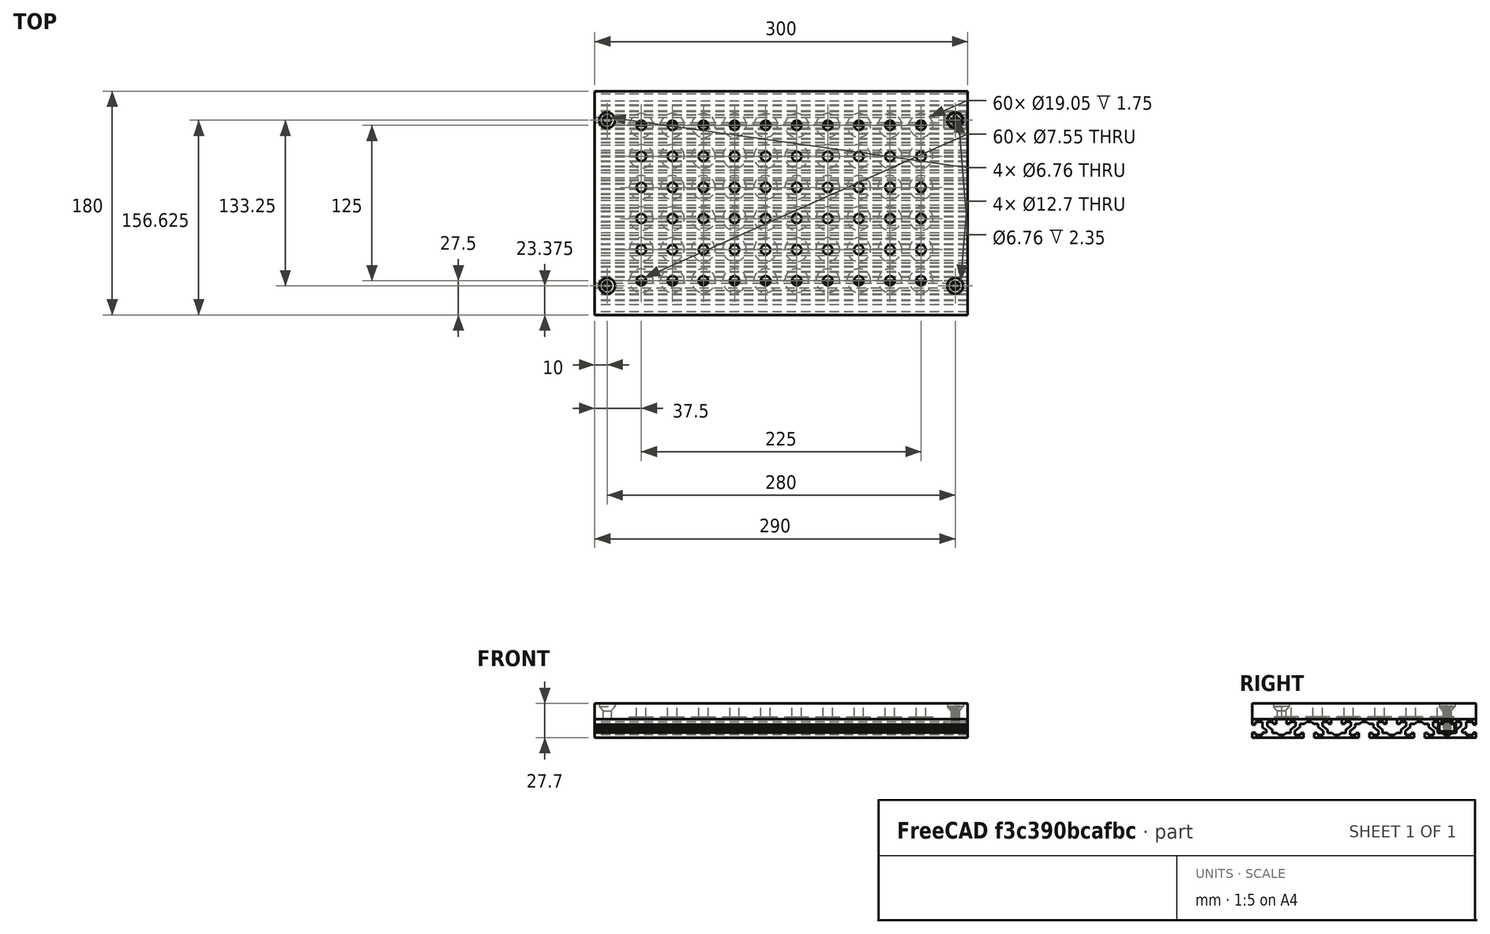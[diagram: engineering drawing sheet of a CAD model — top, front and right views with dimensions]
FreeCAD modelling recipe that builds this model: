
FCSTD DOCUMENT  (FreeCAD 1.0R39109 (Git))
Label: wasteboard
License: All rights reserved
LicenseURL: http://en.wikipedia.org/wiki/All_rights_reserved
objects: Sketcher::SketchObject×11, TechDraw::DrawViewDimension×9, PartDesign::Pocket×5, PartDesign::Pad×4, PartDesign::LinearPattern×4, PartDesign::Chamfer×4, PartDesign::Mirrored×3, PartDesign::Body×3, TechDraw::DrawProjGroupItem×3, PartDesign::Hole×2, PartDesign::MultiTransform×2, TechDraw::DrawSVGTemplate×2, TechDraw::DrawPage×2, Part::Feature×1, PartDesign::ShapeBinder×1, PartDesign::Plane×1, App::Part×1, PartDesign::SubShapeBinder×1, TechDraw::DrawProjGroup×1
note: 110 computed .brp shape members not serialized (recipe doc carries the construction recipe); baked Part::Feature solids carry a one-line shape summary decoded from their .brp

FEATURE [Sketcher::SketchObject] Sketch001
  ArcFitTolerance = 0
  AttachmentSupport = -> [YZ_Plane001]
  FullyConstrained = true
  MakeInternals = false
  MapMode = 5
  Placement = pos=(0,0,0) rot=(0.57735,0.57735,0.57735;2.0944rad)
  sketch-geometry (4):
    g0: LineSegment StartX=-90 StartY=7.5 StartZ=0 EndX=90 EndY=7.5 EndZ=0
    g1: LineSegment StartX=90 StartY=7.5 StartZ=0 EndX=90 EndY=-7.5 EndZ=0
    g2: LineSegment StartX=90 StartY=-7.5 StartZ=0 EndX=-90 EndY=-7.5 EndZ=0
    g3: LineSegment StartX=-90 StartY=-7.5 StartZ=0 EndX=-90 EndY=7.5 EndZ=0
  constraints (10):
    c: Coincident(g0,g1)
    c: Coincident(g1,g2)
    c: Coincident(g2,g3)
    c: Coincident(g3,g0)
    c: Horizontal(g2)
    c: Vertical(g3)
    c: Symmetric(g0,g0,g-2)
    c: Symmetric(g0,g1,g-1)
    c: DistanceX(g0,g0) = 180
    c: DistanceY(g3,g3) = 15
FEATURE [PartDesign::Pad] Pad001
  AllowMultiFace = false
  Direction = (1,0,0)
  Length = 300
  Length2 = 100
  Midplane = true
  Placement = pos=(0,0,0) rot=(0.57735,0.57735,0.57735;2.0944rad)
  Profile = -> Sketch001
  Refine = true
  Suppressed = false
  Type = 0
FEATURE [Sketcher::SketchObject] Sketch002
  ArcFitTolerance = 0
  AttachmentSupport = -> [Pad001]
  ExternalGeometry = -> [Pad001]
  FullyConstrained = true
  MakeInternals = false
  MapMode = 5
  Placement = pos=(150,0,0) rot=(0.57735,0.57735,0.57735;2.0944rad)
  sketch-geometry (14):
    g0: LineSegment StartX=-90 StartY=3.175 StartZ=0 EndX=-87.6 EndY=3.175 EndZ=0
    g1: LineSegment StartX=-87.6 StartY=-3.175 StartZ=0 EndX=-90 EndY=-3.175 EndZ=0
    g2: LineSegment StartX=-90 StartY=-3.175 StartZ=0 EndX=-90 EndY=3.175 EndZ=0
    g3: LineSegment StartX=-87.6 StartY=5.1 StartZ=0 EndX=-82 EndY=5.1 EndZ=0
    g4: LineSegment StartX=-82 StartY=5.1 StartZ=0 EndX=-82 EndY=0.9 EndZ=0
    g5: LineSegment StartX=-82 StartY=-5.1 StartZ=0 EndX=-87.6 EndY=-5.1 EndZ=0
    g6: LineSegment StartX=-87.6 StartY=-5.1 StartZ=0 EndX=-87.6 EndY=-3.175 EndZ=0
    g7: LineSegment StartX=-87.6 StartY=3.175 StartZ=0 EndX=-87.6 EndY=5.1 EndZ=0
    g8: LineSegment [constr] StartX=-87.6 StartY=3.175 StartZ=0 EndX=-87.6 EndY=-3.175 EndZ=0
    g9: LineSegment StartX=-82 StartY=0.9 StartZ=0 EndX=-78.75 EndY=-1.425 EndZ=0
    g10: LineSegment StartX=-78.75 StartY=-1.425 StartZ=0 EndX=-78.75 EndY=-3.175 EndZ=0
    g11: LineSegment StartX=-78.75 StartY=-3.175 StartZ=0 EndX=-82 EndY=-3.175 EndZ=0
    g12: LineSegment StartX=-82 StartY=-3.175 StartZ=0 EndX=-82 EndY=-5.1 EndZ=0
    g13: LineSegment [constr] StartX=-82 StartY=-3.175 StartZ=0 EndX=-87.6 EndY=-3.175 EndZ=0
  constraints (37):
    c: Coincident(g1,g2)
    c: Coincident(g2,g0)
    c: Horizontal(g0)
    c: Horizontal(g1)
    c: Coincident(g3,g4)
    c: Coincident(g12,g5)
    c: Coincident(g5,g6)
    c: Coincident(g7,g3)
    c: Horizontal(g3)
    c: Horizontal(g5)
    c: Vertical(g6)
    c: Coincident(g7,g0)
    c: Vertical(g7)
    c: Coincident(g6,g1)
    c: Symmetric(g0,g1,g-1)
    c: PointOnObject(g0,g-3)
    c: DistanceY(g2,g2) = 6.35
    c: DistanceX(g0,g0) = 2.4
    c: Coincident(g8,g0)
    c: Coincident(g8,g1)
    c: Vertical(g8)
    c: Symmetric(g3,g12,g-1)
    c: DistanceY(g3,g-3) = 2.4
    c: DistanceX(g-3,g3) = 8
    c: Coincident(g10,g9)
    c: Vertical(g10)
    c: Coincident(g11,g10)
    c: Coincident(g4,g9)
    c: Coincident(g12,g11)
    c: Tangent(g4,g12)
    c: DistanceX(g0,g9) = 11.25
    c: DistanceY(g10,g10) = 1.75
    c: Horizontal(g11)
    c: DistanceY(g4,g4) = 4.2
    c: Coincident(g13,g11)
    c: Coincident(g13,g1)
    c: Horizontal(g13)
FEATURE [PartDesign::Pocket] Pocket
  AllowMultiFace = false
  BaseFeature = -> Pad001
  Direction = (-1,0,0)
  Length = 5
  Length2 = 100
  Placement = pos=(0,0,0) rot=(0.57735,0.57735,0.57735;2.0944rad)
  Profile = -> Sketch002
  Refine = true
  Suppressed = false
  Type = 1
FEATURE [PartDesign::Mirrored] Mirrored
  BaseFeature = -> Pocket
  MirrorPlane = -> XZ_Plane001
  Originals = -> [Pocket]
  Placement = pos=(0,0,0) rot=(0.57735,0.57735,0.57735;2.0944rad)
  Refine = true
  Suppressed = false
  TransformMode = 0
FEATURE [Sketcher::SketchObject] Sketch003
  ArcFitTolerance = 0
  AttachmentSupport = -> [Mirrored]
  ExternalGeometry = -> [Mirrored]
  FullyConstrained = true
  MakeInternals = false
  MapMode = 5
  Placement = pos=(150,0,0) rot=(0.57735,0.57735,0.57735;2.0944rad)
  sketch-geometry (28):
    g0: LineSegment StartX=-70.875 StartY=7.5 StartZ=0 EndX=-70.875 EndY=3.5 EndZ=0
    g1: LineSegment StartX=-70.875 StartY=3.5 StartZ=0 EndX=-73.275 EndY=3.5 EndZ=0
    g2: LineSegment StartX=-73.275 StartY=3.5 StartZ=0 EndX=-73.275 EndY=5.1 EndZ=0
    g3: LineSegment StartX=-73.275 StartY=5.1 StartZ=0 EndX=-78 EndY=5.1 EndZ=0
    g4: LineSegment StartX=-78 StartY=5.1 StartZ=0 EndX=-78 EndY=2.1 EndZ=0
    g5: LineSegment StartX=-78 StartY=2.1 StartZ=0 EndX=-74 EndY=-0.972 EndZ=0
    g6: LineSegment StartX=-74 StartY=-0.972 StartZ=0 EndX=-74 EndY=-3.75 EndZ=0
    g7: LineSegment StartX=-74 StartY=-3.75 StartZ=0 EndX=-70.3828 EndY=-3.75 EndZ=0
    g8: LineSegment StartX=-70.3828 StartY=-3.75 StartZ=0 EndX=-68.625 EndY=-5.1 EndZ=0
    g9: LineSegment StartX=-68.625 StartY=-5.1 StartZ=0 EndX=-64.625 EndY=-5.1 EndZ=0
    g10: LineSegment StartX=-62.375 StartY=7.5 StartZ=0 EndX=-70.875 EndY=7.5 EndZ=0
    g11: LineSegment StartX=-62.375 StartY=7.5 StartZ=0 EndX=-62.375 EndY=3.5 EndZ=0
    g12: LineSegment StartX=-62.375 StartY=3.5 StartZ=0 EndX=-59.975 EndY=3.5 EndZ=0
    g13: LineSegment StartX=-59.975 StartY=3.5 StartZ=0 EndX=-59.975 EndY=5.1 EndZ=0
    g14: LineSegment StartX=-59.975 StartY=5.1 StartZ=0 EndX=-55.25 EndY=5.1 EndZ=0
    g15: LineSegment StartX=-55.25 StartY=5.1 StartZ=0 EndX=-55.25 EndY=2.1 EndZ=0
    g16: LineSegment StartX=-55.25 StartY=2.1 StartZ=0 EndX=-59.25 EndY=-0.972 EndZ=0
    g17: LineSegment StartX=-59.25 StartY=-0.972 StartZ=0 EndX=-59.25 EndY=-3.75 EndZ=0
    g18: LineSegment StartX=-59.25 StartY=-3.75 StartZ=0 EndX=-62.8672 EndY=-3.75 EndZ=0
    g19: LineSegment StartX=-62.8672 StartY=-3.75 StartZ=0 EndX=-64.625 EndY=-5.1 EndZ=0
    g20: LineSegment [constr] StartX=-70.3828 StartY=-3.75 StartZ=0 EndX=-62.8672 EndY=-3.75 EndZ=0
    g21: LineSegment [constr] StartX=-70.875 StartY=3.5 StartZ=0 EndX=-62.375 EndY=3.5 EndZ=0
    g22: LineSegment [constr] StartX=-78 StartY=2.1 StartZ=0 EndX=-55.25 EndY=2.1 EndZ=0
    g23: LineSegment [constr] StartX=-59.975 StartY=5.1 StartZ=0 EndX=-73.275 EndY=5.1 EndZ=0
    g24: LineSegment [constr] StartX=-74 StartY=-0.972 StartZ=0 EndX=-59.25 EndY=-0.972 EndZ=0
    g25: LineSegment [constr] StartX=-66.625 StartY=7.5 StartZ=0 EndX=-66.625 EndY=-5.1 EndZ=0
    g26: LineSegment [constr] StartX=-70.3828 StartY=-3.75 StartZ=0 EndX=-74 EndY=-0.972 EndZ=0
    g27: LineSegment [constr] StartX=-62.8672 StartY=-3.75 StartZ=0 EndX=-59.25 EndY=-0.972 EndZ=0
  constraints (76):
    c: PointOnObject(g0,g-3)
    c: Coincident(g1,g0)
    c: Horizontal(g1)
    c: Coincident(g2,g1)
    c: Coincident(g3,g2)
    c: Horizontal(g3)
    c: Coincident(g4,g3)
    c: Coincident(g5,g4)
    c: Coincident(g6,g5)
    c: Coincident(g7,g6)
    c: Coincident(g8,g7)
    c: Coincident(g9,g8)
    c: Horizontal(g9)
    c: PointOnObject(g10,g-3)
    c: Coincident(g10,g0)
    c: Vertical(g0)
    c: Vertical(g2)
    c: Vertical(g6)
    c: Horizontal(g7)
    c: Coincident(g11,g10)
    c: Vertical(g11)
    c: Coincident(g12,g11)
    c: Coincident(g13,g12)
    c: Coincident(g14,g13)
    c: Horizontal(g14)
    c: Coincident(g15,g14)
    c: Vertical(g15)
    c: Coincident(g16,g15)
    c: Coincident(g17,g16)
    c: Vertical(g17)
    c: Coincident(g18,g17)
    c: Horizontal(g18)
    c: Coincident(g19,g18)
    c: Coincident(g19,g9)
    c: Coincident(g20,g7)
    c: Coincident(g20,g18)
    c: Horizontal(g20)
    c: Coincident(g21,g0)
    c: Coincident(g21,g11)
    c: Coincident(g22,g4)
    c: Coincident(g22,g15)
    c: Horizontal(g22)
    c: Coincident(g23,g13)
    c: Coincident(g23,g2)
    c: Horizontal(g23)
    c: Horizontal(g21)
    c: Horizontal(g12)
    c: Vertical(g13)
    c: Vertical(g4)
    c: Coincident(g24,g5)
    c: Coincident(g24,g16)
    c: Horizontal(g24)
    c: DistanceX(g2,g0) = 2.4
    c: Equal(g1,g12)
    c: Vertical(g25)
    c: Symmetric(g9,g8,g25)
    c: Symmetric(g10,g0,g25)
    c: DistanceY(g3,g0) = 2.4
    c: DistanceX(g10,g10) = 8.5
    c: DistanceX(g3,g14) = 22.75
    c: Equal(g14,g3)
    c: DistanceY(g0,g0) = 4
    c: DistanceX(g9,g9) = 4
    c: DistanceX(g6,g17) = 14.75
    c: Equal(g18,g7)
    c: Coincident(g26,g7)
    c: Coincident(g26,g5)
    c: Coincident(g27,g18)
    c: Coincident(g27,g16)
    c: Parallel(g27,g16)
    c: Parallel(g19,g27)
    c: Parallel(g26,g8)
    c: DistanceY(g-4,g8) = 2.4
    c: DistanceY(g4,g4) = 3
    c: DistanceY(g-4,g6) = 3.75
    c: DistanceX(g-5,g3) = 4
FEATURE [PartDesign::Pocket] Pocket001
  AllowMultiFace = false
  BaseFeature = -> Mirrored
  Direction = (-1,0,0)
  Length = 5
  Length2 = 100
  Placement = pos=(0,0,0) rot=(0.57735,0.57735,0.57735;2.0944rad)
  Profile = -> Sketch003
  Refine = true
  Suppressed = false
  Type = 1
FEATURE [PartDesign::LinearPattern] LinearPattern
  BaseFeature = -> Pocket001
  Direction = -> Sketch003 [H_Axis]
  Length = 133.25
  Mode = 0
  Occurrences = 4
  Offset = 44.4167
  Originals = -> [Pocket001]
  Placement = pos=(0,0,0) rot=(0.57735,0.57735,0.57735;2.0944rad)
  Refine = true
  Suppressed = false
  TransformMode = 0
FEATURE [Sketcher::SketchObject] Sketch004
  ArcFitTolerance = 0
  AttachmentSupport = -> [LinearPattern]
  ExternalGeometry = -> [LinearPattern]
  FullyConstrained = true
  MakeInternals = false
  MapMode = 5
  Placement = pos=(150,0,0) rot=(0.57735,0.57735,0.57735;2.0944rad)
  sketch-geometry (30):
    g0: LineSegment StartX=-48.6667 StartY=-7.5 StartZ=0 EndX=-48.6667 EndY=-3.5 EndZ=0
    g1: LineSegment StartX=-48.6667 StartY=-3.5 StartZ=0 EndX=-51.0667 EndY=-3.5 EndZ=0
    g2: LineSegment StartX=-51.0667 StartY=-3.5 StartZ=0 EndX=-51.0667 EndY=-5.1 EndZ=0
    g3: LineSegment StartX=-51.0667 StartY=-5.1 StartZ=0 EndX=-55.7917 EndY=-5.1 EndZ=0
    g4: LineSegment StartX=-55.7917 StartY=-5.1 StartZ=0 EndX=-55.7917 EndY=-2.1 EndZ=0
    g5: LineSegment StartX=-55.7917 StartY=-2.1 StartZ=0 EndX=-51.7917 EndY=0.972 EndZ=0
    g6: LineSegment StartX=-46.4167 StartY=5.1 StartZ=0 EndX=-42.4167 EndY=5.1 EndZ=0
    g7: LineSegment StartX=-42.4167 StartY=5.1 StartZ=0 EndX=-40.6589 EndY=3.75 EndZ=0
    g8: LineSegment StartX=-33.0417 StartY=-2.1 StartZ=0 EndX=-33.0417 EndY=-5.1 EndZ=0
    g9: LineSegment StartX=-33.0417 StartY=-5.1 StartZ=0 EndX=-37.7667 EndY=-5.1 EndZ=0
    g10: LineSegment StartX=-37.7667 StartY=-5.1 StartZ=0 EndX=-37.7667 EndY=-3.5 EndZ=0
    g11: LineSegment StartX=-37.7667 StartY=-3.5 StartZ=0 EndX=-40.1667 EndY=-3.5 EndZ=0
    g12: LineSegment StartX=-40.1667 StartY=-3.5 StartZ=0 EndX=-40.1667 EndY=-7.5 EndZ=0
    g13: LineSegment StartX=-40.1667 StartY=-7.5 StartZ=0 EndX=-48.6667 EndY=-7.5 EndZ=0
    g14: LineSegment [constr] StartX=-44.4167 StartY=-7.5 StartZ=0 EndX=-44.4167 EndY=5.1 EndZ=0
    g15: LineSegment [constr] StartX=-40.1667 StartY=-3.5 StartZ=0 EndX=-48.6667 EndY=-3.5 EndZ=0
    g16: LineSegment [constr] StartX=-37.7667 StartY=-5.1 StartZ=0 EndX=-51.0667 EndY=-5.1 EndZ=0
    g17: LineSegment [constr] StartX=-33.0417 StartY=-2.1 StartZ=0 EndX=-55.7917 EndY=-2.1 EndZ=0
    g18: LineSegment StartX=-51.7917 StartY=0.972 StartZ=0 EndX=-51.7917 EndY=3.75 EndZ=0
    g19: LineSegment StartX=-51.7917 StartY=3.75 StartZ=0 EndX=-48.1745 EndY=3.75 EndZ=0
    g20: LineSegment StartX=-37.0417 StartY=3.75 StartZ=0 EndX=-37.0417 EndY=0.972 EndZ=0
    g21: LineSegment [constr] StartX=-37.0417 StartY=0.972 StartZ=0 EndX=-51.7917 EndY=0.972 EndZ=0
    g22: LineSegment StartX=-37.0417 StartY=0.972 StartZ=0 EndX=-33.0417 EndY=-2.1 EndZ=0
    g23: LineSegment StartX=-48.1745 StartY=3.75 StartZ=0 EndX=-46.4167 EndY=5.1 EndZ=0
    g24: LineSegment StartX=-40.6589 StartY=3.75 StartZ=0 EndX=-37.0417 EndY=3.75 EndZ=0
    g25: LineSegment [constr] StartX=-48.1745 StartY=3.75 StartZ=0 EndX=-40.6589 EndY=3.75 EndZ=0
    g26: LineSegment [constr] StartX=-40.6589 StartY=3.75 StartZ=0 EndX=-37.0417 EndY=0.972 EndZ=0
    g27: LineSegment [constr] StartX=-48.1745 StartY=3.75 StartZ=0 EndX=-51.7917 EndY=0.972 EndZ=0
    g28: LineSegment [constr] StartX=-51.7917 StartY=3.75 StartZ=0 EndX=-55.25 EndY=3.75 EndZ=0
    g29: LineSegment [constr] StartX=-37.0417 StartY=3.75 StartZ=0 EndX=-33.5833 EndY=3.75 EndZ=0
  constraints (82):
    c: PointOnObject(g0,g-3)
    c: Coincident(g1,g0)
    c: Coincident(g2,g1)
    c: Coincident(g3,g2)
    c: Coincident(g4,g3)
    c: Coincident(g5,g4)
    c: Coincident(g6,g23)
    c: Coincident(g7,g6)
    c: Coincident(g8,g22)
    c: Vertical(g8)
    c: Coincident(g9,g8)
    c: Coincident(g10,g9)
    c: Coincident(g11,g10)
    c: Horizontal(g11)
    c: Coincident(g12,g11)
    c: PointOnObject(g12,g-3)
    c: Vertical(g12)
    c: Coincident(g13,g12)
    c: Coincident(g13,g0)
    c: Horizontal(g9)
    c: Horizontal(g3)
    c: Horizontal(g1)
    c: Vertical(g10)
    c: Vertical(g0)
    c: Vertical(g4)
    c: Horizontal(g6)
    c: Vertical(g2)
    c: Vertical(g14)
    c: Coincident(g15,g11)
    c: Coincident(g15,g0)
    c: Coincident(g16,g9)
    c: Coincident(g16,g2)
    c: Coincident(g17,g22)
    c: Coincident(g17,g4)
    c: Horizontal(g17)
    c: Horizontal(g15)
    c: Symmetric(g12,g0,g14)
    c: Symmetric(g6,g23,g14)
    c: DistanceX(g6,g6) = 4
    c: DistanceY(g23,g-4) = 2.4
    c: Equal(g9,g3)
    c: Equal(g2,g10)
    c: DistanceX(g11,g11) = 2.4
    c: DistanceY(g12,g12) = 4
    c: DistanceX(g3,g8) = 22.75
    c: Equal(g11,g1)
    c: DistanceY(g4,g4) = 3
    c: DistanceX(g13,g13) = 8.5
    c: DistanceY(g-3,g3) = 2.4
    c: Vertical(g18)
    c: Coincident(g19,g18)
    c: Horizontal(g19)
    c: Coincident(g20,g24)
    c: Vertical(g20)
    c: Horizontal(g21)
    c: Coincident(g22,g20)
    c: Coincident(g5,g18)
    c: Coincident(g24,g7)
    c: Coincident(g19,g23)
    c: Coincident(g21,g20)
    c: Coincident(g21,g5)
    c: Horizontal(g24)
    c: Coincident(g25,g19)
    c: Coincident(g25,g7)
    c: Horizontal(g25)
    c: Coincident(g26,g7)
    c: Coincident(g26,g20)
    c: Coincident(g27,g19)
    c: Coincident(g27,g5)
    c: Parallel(g27,g23)
    c: Parallel(g27,g5)
    c: Parallel(g7,g26)
    c: Parallel(g26,g22)
    c: DistanceX(g18,g20) = 14.75
    c: DistanceY(g18,g-4) = 3.75
    c: Coincident(g28,g18)
    c: PointOnObject(g28,g-6)
    c: Horizontal(g28)
    c: Coincident(g29,g20)
    c: PointOnObject(g29,g-5)
    c: Horizontal(g29)
    c: Equal(g29,g28)
FEATURE [PartDesign::Pocket] Pocket002
  AllowMultiFace = false
  BaseFeature = -> LinearPattern
  Direction = (-1,0,0)
  Length = 5
  Length2 = 100
  Placement = pos=(0,0,0) rot=(0.57735,0.57735,0.57735;2.0944rad)
  Profile = -> Sketch004
  Refine = true
  Suppressed = false
  Type = 1
FEATURE [PartDesign::LinearPattern] LinearPattern001
  BaseFeature = -> Pocket002
  Direction = -> Sketch004 [H_Axis]
  Length = 88.83
  Mode = 0
  Occurrences = 3
  Offset = 44.415
  Originals = -> [Pocket002]
  Placement = pos=(0,0,0) rot=(0.57735,0.57735,0.57735;2.0944rad)
  Refine = true
  Suppressed = false
  TransformMode = 0
FEATURE [PartDesign::Body] Body001  label="aluminum extruded bed"
  AllowCompound = false
  Group = -> [Sketch001,Pad001,Sketch002,Pocket,Mirrored,Sketch003,Pocket001,LinearPattern,Sketch004,Pocket002,LinearPattern001]
  Origin = -> Origin001
  Tip = -> LinearPattern001
FEATURE [Part::Feature] Part__Feature001  label="90273A540"
  Placement = pos=(140,66.62,14.05) rot=(0,0,1;0rad)
  shape: bbox 12.12 x 12.12 x 19.53 mm, 84 faces (baked)
FEATURE [PartDesign::ShapeBinder] ShapeBinder001
  Placement = pos=(0,0,0) rot=(0.57735,0.57735,0.57735;2.0944rad)
  Support = -> [LinearPattern001]
  TraceSupport = false
FEATURE [PartDesign::Plane] DatumPlane
  AttachmentOffset = pos=(0,0,-10) rot=(0,0,1;0rad)
  AttachmentSupport = -> [ShapeBinder001]
  Length = 60
  MapMode = 5
  Placement = pos=(140,0,0) rot=(0.57735,0.57735,0.57735;2.0944rad)
  ResizeMode = 0
  Width = 60
FEATURE [Sketcher::SketchObject] Sketch008
  ArcFitTolerance = 0
  AttachmentSupport = -> [DatumPlane]
  ExternalGeometry = -> [ShapeBinder001]
  FullyConstrained = true
  MakeInternals = false
  MapMode = 5
  Placement = pos=(140,0,0) rot=(0.57735,0.57735,0.57735;2.0944rad)
  sketch-geometry (8):
    g0: LineSegment StartX=62.525 StartY=5.5 StartZ=0 EndX=70.725 EndY=5.5 EndZ=0
    g1: LineSegment StartX=70.725 StartY=5.5 StartZ=0 EndX=70.725 EndY=3.5 EndZ=0
    g2: LineSegment StartX=62.525 StartY=3.5 StartZ=0 EndX=62.525 EndY=5.5 EndZ=0
    g3: LineSegment StartX=59.4 StartY=3.5 StartZ=0 EndX=62.525 EndY=3.5 EndZ=0
    g4: LineSegment StartX=73.85 StartY=3.5 StartZ=0 EndX=73.85 EndY=-3 EndZ=0
    g5: LineSegment StartX=73.85 StartY=-3 StartZ=0 EndX=59.4 EndY=-3 EndZ=0
    g6: LineSegment StartX=59.4 StartY=-3 StartZ=0 EndX=59.4 EndY=3.5 EndZ=0
    g7: LineSegment StartX=70.725 StartY=3.5 StartZ=0 EndX=73.85 EndY=3.5 EndZ=0
  constraints (24):
    c: Coincident(g0,g1)
    c: Coincident(g2,g0)
    c: Horizontal(g0)
    c: Vertical(g1)
    c: Vertical(g2)
    c: Coincident(g7,g4)
    c: Coincident(g4,g5)
    c: Coincident(g5,g6)
    c: Coincident(g6,g3)
    c: Horizontal(g3)
    c: Horizontal(g5)
    c: Vertical(g4)
    c: Vertical(g6)
    c: Coincident(g3,g2)
    c: Coincident(g7,g1)
    c: DistanceX(g0,g-3) = 0.15
    c: DistanceX(g-4,g0) = 0.15
    c: DistanceX(g-7,g5) = 0.15
    c: DistanceX(g4,g-8) = 0.15
    c: PointOnObject(g-6,g7)
    c: PointOnObject(g-5,g3)
    c: DistanceY(g-8,g4) = 0.75
    c: Horizontal(g7)
    c: DistanceY(g0,g-3) = 2
FEATURE [PartDesign::Pad] Pad002
  AllowMultiFace = false
  Direction = (1,0,0)
  Length = 18
  Length2 = 100
  Midplane = true
  Placement = pos=(140,-1.332e-13,5e-14) rot=(0.57735,0.57735,0.57735;2.0944rad)
  Profile = -> Sketch008
  Refine = true
  Suppressed = false
  Type = 0
FEATURE [Sketcher::SketchObject] Sketch009
  ArcFitTolerance = 0
  AttachmentSupport = -> [Pad002]
  ExternalGeometry = -> [Pad002]
  FullyConstrained = true
  MakeInternals = false
  MapMode = 5
  Placement = pos=(140,-1.332e-13,-3) rot=(0.707107,0.707107,0;3.14159rad)
  sketch-geometry (3):
    g0: Circle CenterX=66.625 CenterY=-3.8e-15 CenterZ=0 NormalX=0 NormalY=0 NormalZ=1 AngleXU=0 Radius=3.3782
    g1: LineSegment [constr] StartX=59.4 StartY=9 StartZ=0 EndX=73.85 EndY=-9 EndZ=0
    g2: LineSegment [constr] StartX=73.85 StartY=9 StartZ=0 EndX=59.4 EndY=-9 EndZ=0
  constraints (7):
    c: Coincident(g1,g-4)
    c: Coincident(g2,g-4)
    c: Coincident(g2,g-3)
    c: Coincident(g1,g-3)
    c: PointOnObject(g0,g2)
    c: PointOnObject(g0,g1)
    c: Diameter(g0) = 6.7564
FEATURE [PartDesign::Pocket] Pocket004
  AllowMultiFace = false
  BaseFeature = -> Pad002
  Direction = (0,0,1)
  Length = 5
  Length2 = 100
  Placement = pos=(140,-1.332e-13,5e-14) rot=(0.57735,0.57735,0.57735;2.0944rad)
  Profile = -> Sketch009
  Refine = true
  Suppressed = false
  Type = 1
FEATURE [Sketcher::SketchObject] Sketch010
  ArcFitTolerance = 0
  AttachmentSupport = -> [Pocket004]
  ExternalGeometry = -> [Pocket004]
  FullyConstrained = true
  MakeInternals = false
  MapMode = 5
  Placement = pos=(140,-1.332e-13,-3) rot=(0.707107,0.707107,0;3.14159rad)
  sketch-geometry (7):
    g0: LineSegment StartX=72.175 StartY=3.20429 StartZ=0 EndX=66.625 EndY=6.40859 EndZ=0
    g1: LineSegment StartX=66.625 StartY=6.40859 StartZ=0 EndX=61.075 EndY=3.20429 EndZ=0
    g2: LineSegment StartX=61.075 StartY=3.20429 StartZ=0 EndX=61.075 EndY=-3.20429 EndZ=0
    g3: LineSegment StartX=61.075 StartY=-3.20429 StartZ=0 EndX=66.625 EndY=-6.40859 EndZ=0
    g4: LineSegment StartX=66.625 StartY=-6.40859 StartZ=0 EndX=72.175 EndY=-3.20429 EndZ=0
    g5: LineSegment StartX=72.175 StartY=-3.20429 StartZ=0 EndX=72.175 EndY=3.20429 EndZ=0
    g6: Circle [constr] CenterX=66.625 CenterY=-2.84e-14 CenterZ=0 NormalX=0 NormalY=0 NormalZ=1 AngleXU=0 Radius=6.40859
  constraints (16):
    c: Coincident(g0,g1)
    c: Coincident(g1,g2)
    c: Coincident(g2,g3)
    c: Coincident(g3,g4)
    c: Coincident(g4,g5)
    c: Coincident(g5,g0)
    c: Equal(g0, g1-g5) x5
    c: PointOnObject(g0,g6)
    c: PointOnObject(g1,g6)
    c: PointOnObject(g2,g6)
    c: PointOnObject(g3,g6)
    c: PointOnObject(g4,g6)
    c: PointOnObject(g5,g6)
    c: Coincident(g6,g-3)
    c: Vertical(g5)
    c: DistanceX(g1,g0) = 11.1
FEATURE [PartDesign::Pocket] Pocket005
  AllowMultiFace = false
  BaseFeature = -> Pocket004
  Direction = (0,0,1)
  Length = 5.95
  Length2 = 100
  Placement = pos=(140,-1.332e-13,5e-14) rot=(0.57735,0.57735,0.57735;2.0944rad)
  Profile = -> Sketch010
  Refine = true
  Suppressed = false
  Type = 0
FEATURE [Sketcher::SketchObject] Sketch011
  ArcFitTolerance = 0
  AttachmentSupport = -> [Pocket005]
  ExternalGeometry = -> [Pocket005]
  FullyConstrained = true
  MakeInternals = false
  MapMode = 5
  Placement = pos=(140,-1.332e-13,2.95) rot=(0.707107,0.707107,0;3.14159rad)
  sketch-geometry (1):
    g0: Circle CenterX=66.625 CenterY=-2.84e-14 CenterZ=0 NormalX=0 NormalY=0 NormalZ=1 AngleXU=0 Radius=3.3782
  constraints (2):
    c: Coincident(g0,g-3)
    c: Equal(g0,g-3)
FEATURE [PartDesign::Pad] Pad003
  AllowMultiFace = false
  BaseFeature = -> Pocket005
  Direction = (0,0,-1)
  Length = 0.2
  Length2 = 100
  Placement = pos=(140,-1.332e-13,5e-14) rot=(0.57735,0.57735,0.57735;2.0944rad)
  Profile = -> Sketch011
  Refine = true
  Reversed = true
  Suppressed = false
  Type = 0
FEATURE [PartDesign::Chamfer] Chamfer
  Angle = 45
  Base = -> Pad003 [Edge28,Edge29,Edge30,Edge31,Edge32,Edge33]
  BaseFeature = -> Pad003
  ChamferType = 0
  FlipDirection = false
  Placement = pos=(140,-1.332e-13,5e-14) rot=(0.57735,0.57735,0.57735;2.0944rad)
  Refine = true
  Size = 1
  Size2 = 1
  SupportTransform = false
  Suppressed = false
  UseAllEdges = false
FEATURE [PartDesign::Chamfer] Chamfer001
  Angle = 45
  Base = -> Chamfer [Edge35,Edge25,Edge24,Edge29]
  BaseFeature = -> Chamfer
  ChamferType = 0
  FlipDirection = false
  Placement = pos=(140,-1.332e-13,5e-14) rot=(0.57735,0.57735,0.57735;2.0944rad)
  Refine = true
  Size = 1
  Size2 = 1
  SupportTransform = false
  Suppressed = false
  UseAllEdges = false
FEATURE [PartDesign::Chamfer] Chamfer002
  Angle = 45
  Base = -> Chamfer001 [Edge26,Edge23,Edge32,Edge29]
  BaseFeature = -> Chamfer001
  ChamferType = 0
  FlipDirection = false
  Placement = pos=(140,-1.332e-13,5e-14) rot=(0.57735,0.57735,0.57735;2.0944rad)
  Refine = true
  Size = 1
  Size2 = 1
  SupportTransform = false
  Suppressed = false
  UseAllEdges = false
FEATURE [PartDesign::Chamfer] Chamfer003
  Angle = 45
  Base = -> Chamfer002 [Edge45,Edge44,Edge43,Edge42,Edge41,Edge40,Edge10,Edge37]
  BaseFeature = -> Chamfer002
  ChamferType = 0
  FlipDirection = false
  Placement = pos=(140,-1.332e-13,5e-14) rot=(0.57735,0.57735,0.57735;2.0944rad)
  Refine = true
  Size = 0.5
  Size2 = 1
  SupportTransform = false
  Suppressed = false
  UseAllEdges = false
FEATURE [PartDesign::Body] Body002  label="3030 1_4-20 tee nut"
  AllowCompound = false
  Group = -> [ShapeBinder001,DatumPlane,Sketch008,Pad002,Sketch009,Pocket004,Sketch010,Pocket005,Sketch011,Pad003,Chamfer,Chamfer001,Chamfer002,Chamfer003]
  Origin = -> Origin003
  Tip = -> Chamfer003
FEATURE [App::Part] Part  label="fasteners"
  Group = -> [Part__Feature001,Body002]
  Origin = -> Origin002
FEATURE [PartDesign::SubShapeBinder] Binder
  BindCopyOnChange = 0
  BindMode = 0
  ClaimChildren = false
  Context = -> Body [Binder.]
  Fuse = false
  MakeFace = true
  OffsetFill = false
  OffsetIntersection = false
  OffsetJoinType = 0
  OffsetOpenResult = false
  PartialLoad = false
  Refine = true
  Relative = true
  Support = -> [Body001[LinearPattern001.Face108,LinearPattern001.Face88]]
  _Version = 2
FEATURE [Sketcher::SketchObject] Sketch
  ArcFitTolerance = 1e-06
  AttachmentSupport = -> [Binder]
  FullyConstrained = true
  MakeInternals = false
  MapMode = 5
  Placement = pos=(0,1.7e-15,7.5) rot=(0,0,1;0rad)
  sketch-geometry (4):
    g0: LineSegment StartX=-150 StartY=90 StartZ=0 EndX=-150 EndY=-90 EndZ=0
    g1: LineSegment StartX=-150 StartY=-90 StartZ=0 EndX=150 EndY=-90 EndZ=0
    g2: LineSegment StartX=150 StartY=-90 StartZ=0 EndX=150 EndY=90 EndZ=0
    g3: LineSegment StartX=150 StartY=90 StartZ=0 EndX=-150 EndY=90 EndZ=0
  constraints (10):
    c: Coincident(g0,g1)
    c: Coincident(g1,g2)
    c: Coincident(g2,g3)
    c: Coincident(g3,g0)
    c: Vertical(g0)
    c: Horizontal(g1)
    c: Symmetric(g2,g0,g-2)
    c: Symmetric(g2,g1,g-1)
    c: DistanceX(g3,g3) = 300
    c: DistanceY(g2,g2) = 180
FEATURE [PartDesign::Pad] Pad
  Direction = (-1.1e-15,0,1)
  Length = 12.7
  Length2 = 10
  Profile = -> Sketch
  ReferenceAxis = -> Sketch [N_Axis]
  Refine = true
  Suppressed = false
  Type = 0
FEATURE [Sketcher::SketchObject] Sketch012
  ArcFitTolerance = 1e-06
  AttachmentSupport = -> [Pad]
  ExternalGeometry = -> [Binder]
  FullyConstrained = true
  MakeInternals = false
  MapMode = 5
  Placement = pos=(-2.24e-14,0,20.2) rot=(0,0,1;0rad)
  sketch-geometry (2):
    g0: Circle CenterX=140 CenterY=66.625 CenterZ=0 NormalX=0 NormalY=0 NormalZ=1 AngleXU=0 Radius=6.35
    g1: LineSegment [constr] StartX=140 StartY=66.625 StartZ=0 EndX=150 EndY=66.625 EndZ=0
  constraints (5):
    c: Diameter(g0) = 12.7
    c: DistanceX(g0,g-3) = 10
    c: Coincident(g1,g0)
    c: Horizontal(g1)
    c: Symmetric(g-3,g-4,g1)
FEATURE [PartDesign::Hole] Hole
  BaseFeature = -> Pad
  CustomThreadClearance = 0
  Depth = 707.177
  DepthType = 1
  Diameter = 6.76
  DrillForDepth = false
  DrillPoint = 1
  DrillPointAngle = 118
  HoleCutCountersinkAngle = 82
  HoleCutCustomValues = false
  HoleCutDepth = 2.54
  HoleCutDiameter = 12.7
  HoleCutType = 3
  ModelThread = false
  Profile = -> Sketch012
  Refine = true
  Suppressed = false
  Tapered = false
  TaperedAngle = 90
  ThreadClass = 0
  ThreadDepth = 707.177
  ThreadDepthType = 0
  ThreadDirection = 0
  ThreadFit = 0
  ThreadSize = 0
  ThreadType = 0
  Threaded = false
  UseCustomThreadClearance = false
FEATURE [PartDesign::Mirrored] Mirrored001
  MirrorPlane = -> Sketch012 [V_Axis]
  Refine = true
  Suppressed = false
  TransformMode = 0
FEATURE [PartDesign::Mirrored] Mirrored002
  MirrorPlane = -> Sketch012 [H_Axis]
  Refine = true
  Suppressed = false
  TransformMode = 0
FEATURE [PartDesign::MultiTransform] MultiTransform
  BaseFeature = -> Hole
  Originals = -> [Hole]
  Refine = true
  Suppressed = false
  TransformMode = 0
  Transformations = -> [Mirrored001,Mirrored002]
FEATURE [Sketcher::SketchObject] Sketch013
  ArcFitTolerance = 1e-06
  AttachmentSupport = -> [MultiTransform]
  ExternalGeometry = -> [MultiTransform]
  FullyConstrained = true
  MakeInternals = false
  MapMode = 5
  Placement = pos=(-8.3e-15,0,7.5) rot=(1,0,0;3.14159rad)
  sketch-geometry (1):
    g0: Circle CenterX=112.5 CenterY=-62.5 CenterZ=0 NormalX=0 NormalY=0 NormalZ=1 AngleXU=0 Radius=9.525
  constraints (3):
    c: Diameter(g0) = 19.05
    c: DistanceX(g0,g-3) = 37.5
    c: DistanceY(g-3,g0) = 27.5
FEATURE [PartDesign::Hole] Hole001
  BaseFeature = -> MultiTransform
  CustomThreadClearance = 0
  Depth = 707.177
  DepthType = 1
  Diameter = 7.55
  DrillForDepth = false
  DrillPoint = 1
  DrillPointAngle = 118
  HoleCutCountersinkAngle = 90
  HoleCutCustomValues = false
  HoleCutDepth = 1.75
  HoleCutDiameter = 19.05
  HoleCutType = 1
  ModelThread = false
  Profile = -> Sketch013
  Refine = true
  Suppressed = false
  Tapered = false
  TaperedAngle = 90
  ThreadClass = 0
  ThreadDepth = 707.177
  ThreadDepthType = 0
  ThreadDirection = 0
  ThreadFit = 0
  ThreadSize = 0
  ThreadType = 0
  Threaded = false
  UseCustomThreadClearance = false
FEATURE [PartDesign::LinearPattern] LinearPattern002
  Direction = -> Sketch013 [H_Axis]
  Length = 225
  Mode = 0
  Occurrences = 10
  Offset = 25
  Refine = true
  Reversed = true
  Suppressed = false
  TransformMode = 0
FEATURE [PartDesign::LinearPattern] LinearPattern003
  Direction = -> Sketch013 [V_Axis]
  Length = 125
  Mode = 0
  Occurrences = 6
  Offset = 25
  Refine = true
  Suppressed = false
  TransformMode = 0
FEATURE [PartDesign::MultiTransform] MultiTransform001
  BaseFeature = -> Hole001
  Originals = -> [Hole001]
  Refine = true
  Suppressed = false
  TransformMode = 0
  Transformations = -> [LinearPattern002,LinearPattern003]
FEATURE [PartDesign::Body] Body  label="wasteboard"
  AllowCompound = false
  Group = -> [Binder,Sketch,Pad,Sketch012,Hole,MultiTransform,Mirrored001,Mirrored002,Sketch013,Hole001,MultiTransform001,LinearPattern002,LinearPattern003]
  Origin = -> Origin
  Tip = -> MultiTransform001
FEATURE [TechDraw::DrawSVGTemplate] Template
  Height = 210
  Orientation = 1
  Template = <path>
  Width = 297
FEATURE [TechDraw::DrawProjGroupItem] View
  CoarseView = false
  Direction = (-2e-16,0,1)
  Focus = 100
  HardHidden = false
  IsoCount = 0
  IsoHidden = false
  IsoVisible = false
  LockPosition = false
  Perspective = false
  Rotation = 0
  RotationVector = (1,0,0)
  Scale = 0.75
  ScaleType = 1
  ScrubCount = 1
  SeamHidden = false
  SeamVisible = false
  SmoothHidden = false
  SmoothVisible = true
  Source = -> [Body]
  Type = 0
  X = 148.5
  XDirection = (-1,0,-2e-16)
  Y = 105
FEATURE [TechDraw::DrawViewDimension] Dimension
  AngleOverride = false
  Arbitrary = false
  ArbitraryTolerances = false
  BoxCorners = (2) [(-112.5,-67.5,0),(112.5,67.5,0)]
  EqualTolerance = true
  ExtensionAngle = 0
  FormatSpec = %.2w mm
  FormatSpecOverTolerance = %+.2w
  FormatSpecUnderTolerance = %+.2w
  Inverted = false
  LineAngle = 0
  LockPosition = false
  MeasureType = 1
  OverTolerance = 0
  References2D = -> [View]
  Rotation = 0
  ScaleType = 0
  TheoreticalExact = false
  Type = 1
  UnderTolerance = 0
  X = 0
  Y = 85.4194
FEATURE [TechDraw::DrawViewDimension] Dimension001
  AngleOverride = false
  Arbitrary = false
  ArbitraryTolerances = false
  BoxCorners = (2) [(-112.5,-67.5,0),(112.5,67.5,0)]
  EqualTolerance = true
  ExtensionAngle = 0
  FormatSpec = %.2w mm
  FormatSpecOverTolerance = %+.2w
  FormatSpecUnderTolerance = %+.2w
  Inverted = false
  LineAngle = 0
  LockPosition = false
  MeasureType = 1
  OverTolerance = 0
  References2D = -> [View]
  Rotation = 0
  ScaleType = 0
  TheoreticalExact = false
  Type = 2
  UnderTolerance = 0
  X = 133.544
  Y = 10.2531
FEATURE [TechDraw::DrawViewDimension] Dimension002
  AngleOverride = false
  Arbitrary = false
  ArbitraryTolerances = false
  BoxCorners = (2) [(-112.5,-67.5,0),(112.5,67.5,0)]
  EqualTolerance = true
  ExtensionAngle = 0
  FormatSpec = %.2w mm
  FormatSpecOverTolerance = %+.2w
  FormatSpecUnderTolerance = %+.2w
  Inverted = false
  LineAngle = 0
  LockPosition = false
  MeasureType = 1
  OverTolerance = 0
  References2D = -> [View]
  Rotation = 0
  ScaleType = 0
  TheoreticalExact = false
  Type = 0
  UnderTolerance = 0
  X = -89.2669
  Y = -81.2709
FEATURE [TechDraw::DrawViewDimension] Dimension003
  AngleOverride = false
  Arbitrary = false
  ArbitraryTolerances = false
  BoxCorners = (2) [(-112.5,-67.5,0),(112.5,67.5,0)]
  EqualTolerance = true
  ExtensionAngle = 0
  FormatSpec = %.2w mm
  FormatSpecOverTolerance = %+.2w
  FormatSpecUnderTolerance = %+.2w
  Inverted = false
  LineAngle = 0
  LockPosition = false
  MeasureType = 1
  OverTolerance = 0
  References2D = -> [View]
  Rotation = 0
  ScaleType = 0
  TheoreticalExact = false
  Type = 0
  UnderTolerance = 0
  X = -135.703
  Y = -31.637
FEATURE [TechDraw::DrawPage] Page  label="wasteboard_page"
  KeepUpdated = true
  NextBalloonIndex = 2
  ProjectionType = 0
  Template = -> Template
  Views = -> [View,Dimension,Dimension001,Dimension002,Dimension003]
FEATURE [TechDraw::DrawSVGTemplate] Template001
  Height = 210
  Orientation = 1
  Template = <path>
  Width = 297
FEATURE [TechDraw::DrawProjGroupItem] View001  label="Front"
  CoarseView = false
  Direction = (0,0,1)
  Focus = 100
  HardHidden = false
  IsoCount = 0
  IsoHidden = false
  IsoVisible = false
  LockPosition = true
  Perspective = false
  Rotation = 0
  RotationVector = (1,0,0)
  Scale = 3
  ScaleType = 2
  ScrubCount = 1
  SeamHidden = false
  SeamVisible = false
  SmoothHidden = false
  SmoothVisible = true
  Source = -> [Body002]
  Type = 0
  X = 0
  XDirection = (-1,-1e-16,0)
  Y = 0
FEATURE [TechDraw::DrawProjGroupItem] ProjItem  label="Left"
  CoarseView = false
  Direction = (1,1e-16,1e-16)
  Focus = 100
  HardHidden = false
  IsoCount = 0
  IsoHidden = false
  IsoVisible = false
  LockPosition = false
  Perspective = false
  Rotation = 0
  RotationVector = (1,0,0)
  Scale = 3
  ScaleType = 2
  ScrubCount = 1
  SeamHidden = false
  SeamVisible = false
  SmoothHidden = false
  SmoothVisible = true
  Source = -> [Body002]
  Type = 1
  X = 54.75
  XDirection = (-1e-16,0,1)
  Y = 0
FEATURE [TechDraw::DrawProjGroup] ProjGroup
  Anchor = -> View001
  AutoDistribute = true
  LockPosition = false
  ProjectionType = 0
  Rotation = 0
  Scale = 3
  ScaleType = 1
  Source = -> [Body002]
  Views = -> [View001,ProjItem]
  X = 148.5
  Y = 105
  spacingX = 15
  spacingY = 15
FEATURE [TechDraw::DrawViewDimension] Dimension004
  AngleOverride = false
  Arbitrary = false
  ArbitraryTolerances = false
  BoxCorners = (2) [(-27,-21.675,0),(27,21.675,0)]
  EqualTolerance = true
  ExtensionAngle = 0
  FormatSpec = %.2w mm
  FormatSpecOverTolerance = %+.2w
  FormatSpecUnderTolerance = %+.2w
  Inverted = false
  LineAngle = 0
  LockPosition = false
  MeasureType = 1
  OverTolerance = 0
  References2D = -> [View001]
  Rotation = 0
  ScaleType = 0
  TheoreticalExact = false
  Type = 1
  UnderTolerance = 0
  X = 0
  Y = 33.0354
FEATURE [TechDraw::DrawViewDimension] Dimension005
  AngleOverride = false
  Arbitrary = false
  ArbitraryTolerances = false
  BoxCorners = (2) [(-27,-21.675,0),(27,21.675,0)]
  EqualTolerance = true
  ExtensionAngle = 0
  FormatSpec = %.2w mm
  FormatSpecOverTolerance = %+.2w
  FormatSpecUnderTolerance = %+.2w
  Inverted = false
  LineAngle = 0
  LockPosition = false
  MeasureType = 1
  OverTolerance = 0
  References2D = -> [View001]
  Rotation = 0
  ScaleType = 0
  TheoreticalExact = false
  Type = 2
  UnderTolerance = 0
  X = -41.5077
  Y = 0
FEATURE [TechDraw::DrawViewDimension] Dimension006
  AngleOverride = false
  Arbitrary = false
  ArbitraryTolerances = false
  BoxCorners = (2) [(-12.75,-21.675,0),(12.75,21.675,0)]
  EqualTolerance = true
  ExtensionAngle = 0
  FormatSpec = %.2w mm
  FormatSpecOverTolerance = %+.2w
  FormatSpecUnderTolerance = %+.2w
  Inverted = false
  LineAngle = 0
  LockPosition = false
  MeasureType = 1
  OverTolerance = 0
  References2D = -> [ProjItem]
  Rotation = 0
  ScaleType = 0
  TheoreticalExact = false
  Type = 2
  UnderTolerance = 0
  X = 27.1235
  Y = 0
FEATURE [TechDraw::DrawViewDimension] Dimension007
  AngleOverride = false
  Arbitrary = false
  ArbitraryTolerances = false
  BoxCorners = (2) [(-12.75,-21.675,0),(12.75,21.675,0)]
  EqualTolerance = true
  ExtensionAngle = 0
  FormatSpec = %.2w mm
  FormatSpecOverTolerance = %+.2w
  FormatSpecUnderTolerance = %+.2w
  Inverted = false
  LineAngle = 0
  LockPosition = false
  MeasureType = 1
  OverTolerance = 0
  References2D = -> [ProjItem]
  Rotation = 0
  ScaleType = 0
  TheoreticalExact = false
  Type = 1
  UnderTolerance = 0
  X = 24.5406
  Y = 40.9628
FEATURE [TechDraw::DrawViewDimension] Dimension008
  AngleOverride = false
  Arbitrary = false
  ArbitraryTolerances = false
  BoxCorners = (2) [(-12.75,-21.675,0),(12.75,21.675,0)]
  EqualTolerance = true
  ExtensionAngle = 0
  FormatSpec = %.2w mm
  FormatSpecOverTolerance = %+.2w
  FormatSpecUnderTolerance = %+.2w
  Inverted = false
  LineAngle = 0
  LockPosition = false
  MeasureType = 1
  OverTolerance = 0
  References2D = -> [ProjItem]
  Rotation = 0
  ScaleType = 0
  TheoreticalExact = false
  Type = 1
  UnderTolerance = 0
  X = 25.1319
  Y = 32.2593
FEATURE [TechDraw::DrawPage] Page001  label="t-slot_nut_page"
  KeepUpdated = true
  NextBalloonIndex = 1
  ProjectionType = 0
  Template = -> Template001
  Views = -> [ProjGroup,Dimension004,Dimension005,Dimension006,Dimension007,Dimension008]
note: 2 file-system paths scrubbed to <path> (originals preserved in the JSON sidecar)
